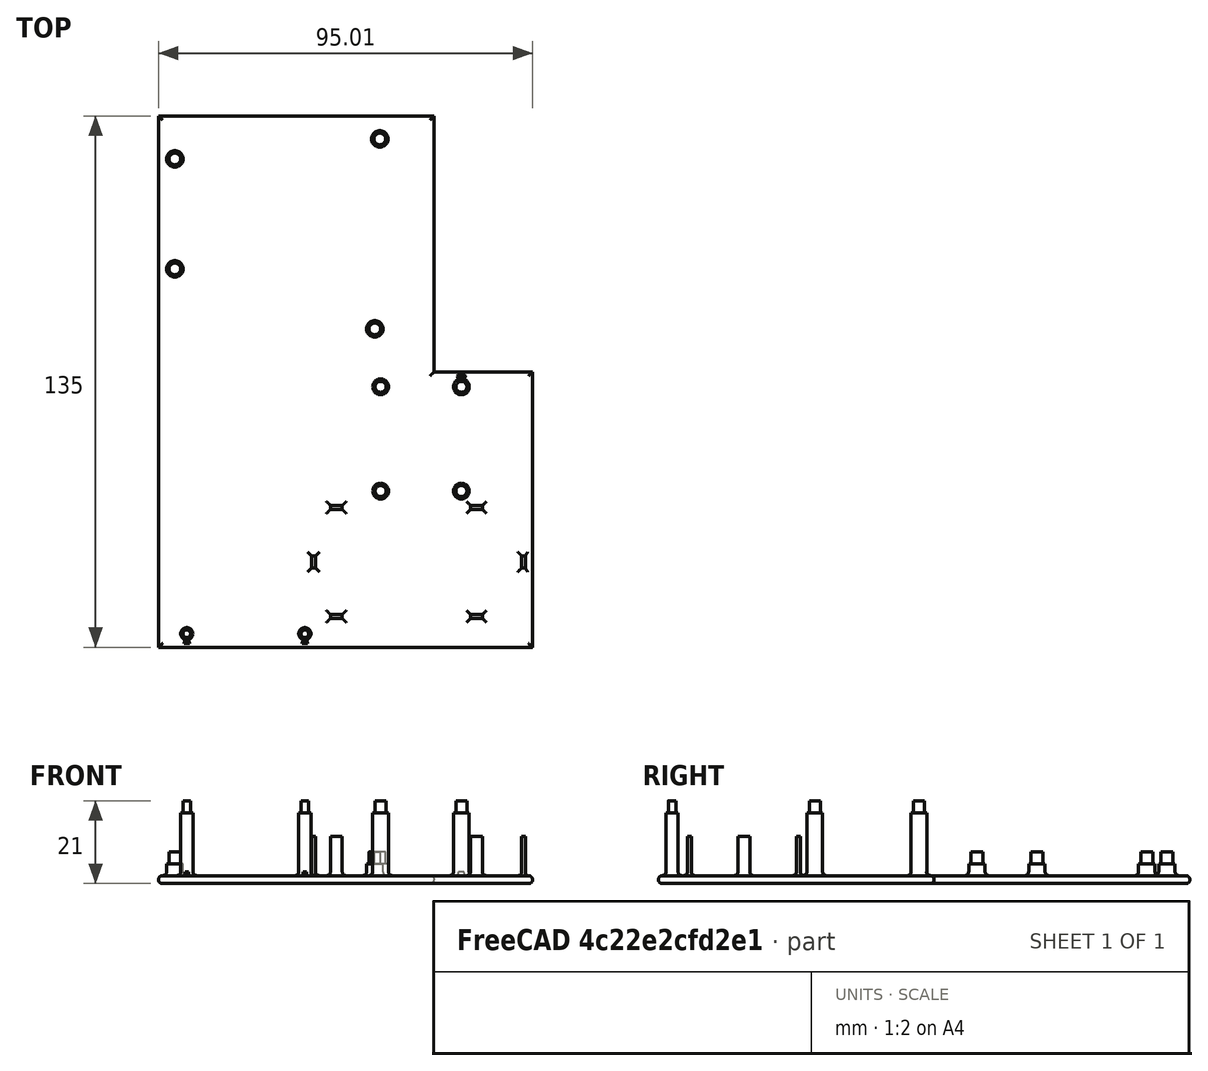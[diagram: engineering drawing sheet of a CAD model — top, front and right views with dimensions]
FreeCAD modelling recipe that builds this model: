
FCSTD DOCUMENT  (FreeCAD 2024.104R38929 (Git))
Label: arduino_tetris_platform
License: All rights reserved
objects: Part::SubShapeBinder×28, Sketcher::SketchObject×17, PartDesign::Pad×14, PartDesign::Fillet×5, PartDesign::Plane×3, PartDesign::Body×2, Mesh::Feature×2, PartDesign::Pocket×1, App::Part×1
note: 127 computed .brp shape members not serialized (recipe doc carries the construction recipe); baked Part::Feature solids carry a one-line shape summary decoded from their .brp

FEATURE [PartDesign::Plane] DatumPlane  label="PlaneBottomPlacholder"
  AttachmentOffset = pos=(0,0,4.5) rot=(0,0,1;0rad)
  InvalidShape = false
  Length = 101.325
  MapMode = 1
  MinimumLength = 10
  MinimumWidth = 10
  Placement = pos=(-3.175,-4.2,-4.295) rot=(0,0,1;0rad)
  ResizeMode = 0
  TreeRank = 432
  ValidateShape = false
  Width = 184.339
FEATURE [Sketcher::SketchObject] Sketch001
  ArcFitTolerance = 1e-06
  AttachmentSupport = -> [DatumPlane]
  ExternalBSplineMaxDegree = 5
  ExternalBSplineTolerance = 0.0001
  FullyConstrained = false
  InternalTolerance = 1e-06
  InvalidShape = false
  MakeInternals = false
  MapMode = 5
  Placement = pos=(-3.175,-4.2,-4.295) rot=(0,0,1;0rad)
  Support = -> [DatumPlane]
  TreeRank = 443
  ValidateShape = false
  sketch-geometry (4):
    g0: LineSegment StartX=-107.22 StartY=0 StartZ=0 EndX=46.1072 EndY=0 EndZ=0
    g1: LineSegment StartX=46.1072 StartY=0 StartZ=0 EndX=46.1072 EndY=144.523 EndZ=0
    g2: LineSegment StartX=46.1072 StartY=144.523 StartZ=0 EndX=-107.22 EndY=144.523 EndZ=0
    g3: LineSegment StartX=-107.22 StartY=144.523 StartZ=0 EndX=-107.22 EndY=0 EndZ=0
  constraints (9):
    c: Coincident(g0,g1)
    c: Coincident(g1,g2)
    c: Coincident(g2,g3)
    c: Coincident(g3,g0)
    c: Horizontal(g0)
    c: Horizontal(g2)
    c: Vertical(g1)
    c: Vertical(g3)
    c: PointOnObject(g0,g-1)
FEATURE [PartDesign::Plane] DatumPlane001  label="PlaneTopPlaceholder"
  AttachmentOffset = pos=(0,0,16) rot=(0,0,1;0rad)
  InvalidShape = false
  Length = 101.325
  MapMode = 5
  MinimumLength = 10
  MinimumWidth = 10
  Placement = pos=(0,0,24.75) rot=(0,0,1;0rad)
  ResizeMode = 0
  TreeRank = 444
  ValidateShape = false
  Width = 184.339
FEATURE [Sketcher::SketchObject] Sketch002
  ArcFitTolerance = 1e-06
  AttachmentSupport = -> [DatumPlane001]
  ExternalBSplineMaxDegree = 5
  ExternalBSplineTolerance = 0.0001
  FullyConstrained = false
  InternalTolerance = 1e-06
  InvalidShape = false
  MakeInternals = false
  MapMode = 5
  Placement = pos=(0,0,24.75) rot=(0,0,1;0rad)
  Support = -> [DatumPlane001]
  TreeRank = 445
  ValidateShape = false
  sketch-geometry (4):
    g0: LineSegment StartX=-110.57 StartY=-4.40204 StartZ=0 EndX=43.0268 EndY=-4.40204 EndZ=0
    g1: LineSegment StartX=43.0268 StartY=-4.40204 StartZ=0 EndX=43.0268 EndY=140.417 EndZ=0
    g2: LineSegment StartX=43.0268 StartY=140.417 StartZ=0 EndX=-110.57 EndY=140.417 EndZ=0
    g3: LineSegment StartX=-110.57 StartY=140.417 StartZ=0 EndX=-110.57 EndY=-4.40204 EndZ=0
  constraints (8):
    c: Coincident(g0,g1)
    c: Coincident(g1,g2)
    c: Coincident(g2,g3)
    c: Coincident(g3,g0)
    c: Horizontal(g0)
    c: Horizontal(g2)
    c: Vertical(g1)
    c: Vertical(g3)
FEATURE [PartDesign::Body] Body001  label="Visualisation"
  AutoGroupSolids = false
  ClaimAllChildren = false
  ExportMode = 0
  Group = -> [Sketch001,Sketch002]
  InvalidShape = false
  Origin = -> Origin010
  TreeRank = 442
  ValidateShape = false
  _ExportChildren = -> [Sketch001,Sketch002]
  _GroupVersion = 1
FEATURE [PartDesign::Plane] DatumPlane002  label="PlaneBottom"
  AttachmentOffset = pos=(0,0,-2) rot=(0,0,1;0rad)
  AttachmentSupport = -> [DatumPlane]
  InvalidShape = false
  Length = 101.325
  MapMode = 5
  MinimumLength = 10
  MinimumWidth = 10
  Placement = pos=(-3.175,-4.2,-6.295) rot=(0,0,1;0rad)
  ResizeMode = 0
  Support = -> [DatumPlane]
  TreeRank = 477
  ValidateShape = false
  Width = 184.339
FEATURE [Sketcher::SketchObject] Sketch005
  ArcFitTolerance = 1e-06
  AttachmentSupport = -> [DatumPlane002]
  ExternalBSplineMaxDegree = 5
  ExternalBSplineTolerance = 0.0001
  FullyConstrained = true
  InternalTolerance = 1e-06
  InvalidShape = false
  MakeInternals = false
  MapMode = 5
  Placement = pos=(-3.175,-4.2,-6.295) rot=(0,0,1;0rad)
  Support = -> [DatumPlane002]
  TreeRank = 491
  ValidateShape = false
  sketch-geometry (4):
    g0: LineSegment StartX=0 StartY=0 StartZ=0 EndX=95 EndY=0 EndZ=0
    g1: LineSegment StartX=95 StartY=0 StartZ=0 EndX=95 EndY=135 EndZ=0
    g2: LineSegment StartX=95 StartY=135 StartZ=0 EndX=0 EndY=135 EndZ=0
    g3: LineSegment StartX=0 StartY=135 StartZ=0 EndX=0 EndY=0 EndZ=0
  constraints (11):
    c: Coincident(g0,g1)
    c: Coincident(g1,g2)
    c: Coincident(g2,g3)
    c: Coincident(g3,g0)
    c: Horizontal(g0)
    c: Horizontal(g2)
    c: Vertical(g1)
    c: Vertical(g3)
    c: Coincident(g0,g-1)
    c: DistanceX(g2,g2) = 95
    c: DistanceY(g1,g1) = 135
FEATURE [PartDesign::Pad] Pad002
  AddSubType = 0
  AlongSketchNormal = false
  AutoTaperInnerAngle = true
  CheckUpToFaceLimits = true
  ClaimChildren = false
  Direction = (0,0,1)
  Fit = 0
  FitJoin = 0
  InnerFit = 0
  InnerFitJoin = 0
  InvalidShape = false
  Length = 2
  Length2 = 10
  Linearize = true
  NewSolid = false
  Profile = -> Sketch005
  ReferenceAxis = -> Sketch005 [N_Axis]
  Suppress = false
  TaperInnerAngle = 0
  TaperInnerAngleRev = 0
  TreeRank = 492
  Type = 0
  ValidateShape = false
  _ProfileBasedVersion = 1
FEATURE [Part::SubShapeBinder] Import  label="Import(1e77-TFT-160x128)"
  BindCopyOnChange = 0
  BindMode = 0
  ClaimChildren = false
  Context = -> Part010 [Body003.Import.]
  EdgeTolerance = 1e-06
  FillStyle = 0
  Fuse = false
  InvalidShape = false
  MakeFace = false
  MergeEdges = true
  OffsetFill = false
  OffsetIntersection = false
  OffsetJoinType = 0
  OffsetOpenResult = false
  Outline = false
  PartialLoad = false
  Relative = true
  SplitEdges = false
  TightBound = false
  TreeRank = 494
  ValidateShape = false
  _Version = 8
FEATURE [Part::SubShapeBinder] Import001  label="Import001(1e77-TFT-160x128)"
  BindCopyOnChange = 0
  BindMode = 0
  ClaimChildren = false
  Context = -> Part010 [Body003.Import001.]
  EdgeTolerance = 1e-06
  FillStyle = 0
  Fuse = false
  InvalidShape = false
  MakeFace = false
  MergeEdges = true
  OffsetFill = false
  OffsetIntersection = false
  OffsetJoinType = 0
  OffsetOpenResult = false
  Outline = false
  PartialLoad = false
  Relative = true
  SplitEdges = false
  TightBound = false
  TreeRank = 495
  ValidateShape = false
  _Version = 8
FEATURE [Part::SubShapeBinder] Import002  label="Import002(PCB)"
  BindCopyOnChange = 0
  BindMode = 0
  ClaimChildren = false
  Context = -> Part010 [Body003.Import002.]
  EdgeTolerance = 1e-06
  FillStyle = 0
  Fuse = false
  InvalidShape = false
  MakeFace = false
  MergeEdges = true
  OffsetFill = false
  OffsetIntersection = false
  OffsetJoinType = 0
  OffsetOpenResult = false
  Outline = false
  PartialLoad = false
  Relative = true
  SplitEdges = false
  TightBound = false
  TreeRank = 496
  ValidateShape = false
  _Version = 8
FEATURE [Part::SubShapeBinder] Import003  label="Import003(PCB)"
  BindCopyOnChange = 0
  BindMode = 0
  ClaimChildren = false
  Context = -> Part010 [Body003.Import003.]
  EdgeTolerance = 1e-06
  FillStyle = 0
  Fuse = false
  InvalidShape = false
  MakeFace = false
  MergeEdges = true
  OffsetFill = false
  OffsetIntersection = false
  OffsetJoinType = 0
  OffsetOpenResult = false
  Outline = false
  PartialLoad = false
  Relative = true
  SplitEdges = false
  TightBound = false
  TreeRank = 497
  ValidateShape = false
  _Version = 8
FEATURE [Part::SubShapeBinder] Import004  label="Import004(PCB)"
  BindCopyOnChange = 0
  BindMode = 0
  ClaimChildren = false
  Context = -> Part010 [Body003.Import004.]
  EdgeTolerance = 1e-06
  FillStyle = 0
  Fuse = false
  InvalidShape = false
  MakeFace = false
  MergeEdges = true
  OffsetFill = false
  OffsetIntersection = false
  OffsetJoinType = 0
  OffsetOpenResult = false
  Outline = false
  PartialLoad = false
  Relative = true
  SplitEdges = false
  TightBound = false
  TreeRank = 498
  ValidateShape = false
  _Version = 8
FEATURE [Part::SubShapeBinder] Import005  label="Import005(PCB)"
  BindCopyOnChange = 0
  BindMode = 0
  ClaimChildren = false
  Context = -> Part010 [Body003.Import005.]
  EdgeTolerance = 1e-06
  FillStyle = 0
  Fuse = false
  InvalidShape = false
  MakeFace = false
  MergeEdges = true
  OffsetFill = false
  OffsetIntersection = false
  OffsetJoinType = 0
  OffsetOpenResult = false
  Outline = false
  PartialLoad = false
  Relative = true
  SplitEdges = false
  TightBound = false
  TreeRank = 499
  ValidateShape = false
  _Version = 8
FEATURE [Sketcher::SketchObject] Sketch006
  ArcFitTolerance = 1e-06
  AttachmentSupport = -> [Pad002]
  ExternalBSplineMaxDegree = 5
  ExternalBSplineTolerance = 0.0001
  ExternalGeometry = -> [Import,Import001,Import002,Import003,Import004,Import005]
  FullyConstrained = true
  InternalTolerance = 1e-06
  InvalidShape = false
  MakeInternals = false
  MapMode = 5
  Placement = pos=(0,0,-4.295) rot=(0,0,1;0rad)
  Support = -> [Pad002]
  TreeRank = 514
  ValidateShape = false
  sketch-geometry (18):
    g0: Circle CenterX=4 CenterY=-0.75 CenterZ=0 NormalX=0 NormalY=0 NormalZ=1 AngleXU=0 Radius=1.55
    g1: Circle CenterX=34 CenterY=-0.75 CenterZ=0 NormalX=0 NormalY=0 NormalZ=1 AngleXU=0 Radius=1.55
    g2: Circle CenterX=53.25 CenterY=35.5 CenterZ=0 NormalX=0 NormalY=0 NormalZ=1 AngleXU=0 Radius=2
    g3: Circle CenterX=53.25 CenterY=62 CenterZ=0 NormalX=0 NormalY=0 NormalZ=1 AngleXU=0 Radius=2
    g4: Circle CenterX=73.75 CenterY=62 CenterZ=0 NormalX=0 NormalY=0 NormalZ=1 AngleXU=0 Radius=2
    g5: Circle CenterX=73.75 CenterY=35.5 CenterZ=0 NormalX=0 NormalY=0 NormalZ=1 AngleXU=0 Radius=2
    g6: GeomPoint [constr] X=5.55 Y=-0.75 Z=0
    g7: GeomPoint [constr] X=5.05 Y=-0.75 Z=0
    g8: GeomPoint [constr] X=35.55 Y=-0.75 Z=0
    g9: GeomPoint [constr] X=35.05 Y=-0.75 Z=0
    g10: GeomPoint [constr] X=55.25 Y=35.5 Z=0
    g11: GeomPoint [constr] X=54.75 Y=35.5 Z=0
    g12: GeomPoint [constr] X=75.75 Y=35.5 Z=0
    g13: GeomPoint [constr] X=75.25 Y=35.5 Z=0
    g14: GeomPoint [constr] X=75.75 Y=62 Z=0
    g15: GeomPoint [constr] X=75.25 Y=62 Z=0
    g16: GeomPoint [constr] X=55.25 Y=62 Z=0
    g17: GeomPoint [constr] X=54.75 Y=62 Z=0
  constraints (36):
    c: Coincident(g-3,g0)
    c: Coincident(g1,g-4)
    c: Coincident(g-5,g2)
    c: Coincident(g5,g-6)
    c: Coincident(g4,g-7)
    c: Coincident(g3,g-8)
    c: PointOnObject(g6,g0)
    c: PointOnObject(g7,g-3)
    c: Horizontal(g0,g6)
    c: Horizontal(g6,g7)
    c: PointOnObject(g8,g1)
    c: PointOnObject(g9,g-4)
    c: Horizontal(g8,g9)
    c: Horizontal(g9,g1)
    c: PointOnObject(g10,g2)
    c: PointOnObject(g11,g-5)
    c: Horizontal(g11,g10)
    c: Horizontal(g10,g2)
    c: PointOnObject(g12,g5)
    c: PointOnObject(g13,g-6)
    c: Horizontal(g13,g12)
    c: Horizontal(g12,g5)
    c: PointOnObject(g14,g4)
    c: PointOnObject(g15,g-7)
    c: Horizontal(g15,g14)
    c: Horizontal(g14,g4)
    c: PointOnObject(g16,g3)
    c: PointOnObject(g17,g-8)
    c: Horizontal(g17,g16)
    c: Horizontal(g16,g3)
    c: DistanceX(g7,g6) = 0.5
    c: DistanceX(g9,g8) = 0.5
    c: DistanceX(g11,g10) = 0.5
    c: DistanceX(g13,g12) = 0.5
    c: DistanceX(g15,g14) = 0.5
    c: DistanceX(g17,g16) = 0.5
FEATURE [Part::SubShapeBinder] Import006  label="Import006(arduino_uno)"
  BindCopyOnChange = 0
  BindMode = 0
  ClaimChildren = false
  Context = -> Part010 [Body003.Import006.]
  EdgeTolerance = 1e-06
  FillStyle = 0
  Fuse = false
  InvalidShape = false
  MakeFace = false
  MergeEdges = true
  OffsetFill = false
  OffsetIntersection = false
  OffsetJoinType = 0
  OffsetOpenResult = false
  Outline = false
  PartialLoad = false
  Relative = true
  SplitEdges = false
  TightBound = false
  TreeRank = 500
  ValidateShape = false
  _Version = 8
FEATURE [Part::SubShapeBinder] Import007  label="Import007(arduino_uno)"
  BindCopyOnChange = 0
  BindMode = 0
  ClaimChildren = false
  Context = -> Part010 [Body003.Import007.]
  EdgeTolerance = 1e-06
  FillStyle = 0
  Fuse = false
  InvalidShape = false
  MakeFace = false
  MergeEdges = true
  OffsetFill = false
  OffsetIntersection = false
  OffsetJoinType = 0
  OffsetOpenResult = false
  Outline = false
  PartialLoad = false
  Relative = true
  SplitEdges = false
  TightBound = false
  TreeRank = 501
  ValidateShape = false
  _Version = 8
FEATURE [Part::SubShapeBinder] Import008  label="Import008(arduino_uno)"
  BindCopyOnChange = 0
  BindMode = 0
  ClaimChildren = false
  Context = -> Part010 [Body003.Import008.]
  EdgeTolerance = 1e-06
  FillStyle = 0
  Fuse = false
  InvalidShape = false
  MakeFace = false
  MergeEdges = true
  OffsetFill = false
  OffsetIntersection = false
  OffsetJoinType = 0
  OffsetOpenResult = false
  Outline = false
  PartialLoad = false
  Relative = true
  SplitEdges = false
  TightBound = false
  TreeRank = 502
  ValidateShape = false
  _Version = 8
FEATURE [Part::SubShapeBinder] Import009  label="Import009(arduino_uno)"
  BindCopyOnChange = 0
  BindMode = 0
  ClaimChildren = false
  Context = -> Part010 [Body003.Import009.]
  EdgeTolerance = 1e-06
  FillStyle = 0
  Fuse = false
  InvalidShape = false
  MakeFace = false
  MergeEdges = true
  OffsetFill = false
  OffsetIntersection = false
  OffsetJoinType = 0
  OffsetOpenResult = false
  Outline = false
  PartialLoad = false
  Relative = true
  SplitEdges = false
  TightBound = false
  TreeRank = 503
  ValidateShape = false
  _Version = 8
FEATURE [Part::SubShapeBinder] Import010  label="Import010(9V_Battery)"
  BindCopyOnChange = 0
  BindMode = 0
  ClaimChildren = false
  Context = -> Part010 [Body003.Import010.]
  EdgeTolerance = 1e-06
  FillStyle = 0
  Fuse = false
  InvalidShape = false
  MakeFace = false
  MergeEdges = true
  OffsetFill = false
  OffsetIntersection = false
  OffsetJoinType = 0
  OffsetOpenResult = false
  Outline = false
  PartialLoad = false
  Relative = true
  SplitEdges = false
  TightBound = false
  TreeRank = 504
  ValidateShape = false
  _Version = 8
FEATURE [Part::SubShapeBinder] Import011  label="Import011(9V Battery Clip Connector)"
  BindCopyOnChange = 0
  BindMode = 0
  ClaimChildren = false
  Context = -> Part010 [Body003.Import011.]
  EdgeTolerance = 1e-06
  FillStyle = 0
  Fuse = false
  InvalidShape = false
  MakeFace = false
  MergeEdges = true
  OffsetFill = false
  OffsetIntersection = false
  OffsetJoinType = 0
  OffsetOpenResult = false
  Outline = false
  PartialLoad = false
  Relative = true
  SplitEdges = false
  TightBound = false
  TreeRank = 505
  ValidateShape = false
  _Version = 8
FEATURE [Part::SubShapeBinder] Import012  label="Import012(9V_Battery)"
  BindCopyOnChange = 0
  BindMode = 0
  ClaimChildren = false
  Context = -> Part010 [Body003.Import012.]
  EdgeTolerance = 1e-06
  FillStyle = 0
  Fuse = false
  InvalidShape = false
  MakeFace = false
  MergeEdges = true
  OffsetFill = false
  OffsetIntersection = false
  OffsetJoinType = 0
  OffsetOpenResult = false
  Outline = false
  PartialLoad = false
  Relative = true
  SplitEdges = false
  TightBound = false
  TreeRank = 506
  ValidateShape = false
  _Version = 8
FEATURE [Part::SubShapeBinder] Import013  label="Import013(9V_Battery)"
  BindCopyOnChange = 0
  BindMode = 0
  ClaimChildren = false
  Context = -> Part010 [Body003.Import013.]
  EdgeTolerance = 1e-06
  FillStyle = 0
  Fuse = false
  InvalidShape = false
  MakeFace = false
  MergeEdges = true
  OffsetFill = false
  OffsetIntersection = false
  OffsetJoinType = 0
  OffsetOpenResult = false
  Outline = false
  PartialLoad = false
  Relative = true
  SplitEdges = false
  TightBound = false
  TreeRank = 507
  ValidateShape = false
  _Version = 8
FEATURE [Sketcher::SketchObject] Sketch007
  ArcFitTolerance = 1e-06
  AttachmentSupport = -> [Pad002]
  ExternalBSplineMaxDegree = 5
  ExternalBSplineTolerance = 0.0001
  ExternalGeometry = -> [Import006,Import007,Import008,Import009]
  FullyConstrained = true
  InternalTolerance = 1e-06
  InvalidShape = false
  MakeInternals = false
  MapMode = 5
  Placement = pos=(0,0,-4.295) rot=(0,0,1;0rad)
  Support = -> [Pad002]
  TreeRank = 513
  ValidateShape = false
  sketch-geometry (8):
    g0: Circle CenterX=51.76 CenterY=76.7 CenterZ=0 NormalX=0 NormalY=0 NormalZ=1 AngleXU=0 Radius=2.0875
    g1: Circle CenterX=0.96 CenterY=91.94 CenterZ=0 NormalX=0 NormalY=0 NormalZ=1 AngleXU=0 Radius=2.0875
    g2: Circle CenterX=0.96 CenterY=119.88 CenterZ=0 NormalX=0 NormalY=0 NormalZ=1 AngleXU=0 Radius=2.0875
    g3: Circle CenterX=53.03 CenterY=124.96 CenterZ=0 NormalX=0 NormalY=0 NormalZ=1 AngleXU=0 Radius=2.0875
    g4: GeomPoint [constr] X=53.8475 Y=76.7 Z=0
    g5: GeomPoint [constr] X=3.0475 Y=91.94 Z=0
    g6: GeomPoint [constr] X=3.0475 Y=119.88 Z=0
    g7: GeomPoint [constr] X=55.1175 Y=124.96 Z=0
  constraints (16):
    c: Coincident(g-3,g0)
    c: Coincident(g-6,g3)
    c: Coincident(g2,g-5)
    c: Coincident(g-4,g1)
    c: PointOnObject(g4,g0)
    c: Horizontal(g4,g-3)
    c: PointOnObject(g5,g1)
    c: Horizontal(g5,g-4)
    c: PointOnObject(g6,g2)
    c: Horizontal(g6,g-5)
    c: PointOnObject(g7,g3)
    c: Horizontal(g7,g-6)
    c: DistanceX(g-3,g4) = 0.5
    c: DistanceX(g-6,g7) = 0.5
    c: DistanceX(g-4,g5) = 0.5
    c: DistanceX(g-5,g6) = 0.5
FEATURE [PartDesign::Pad] Pad003
  AddSubType = 0
  AlongSketchNormal = false
  AutoTaperInnerAngle = true
  BaseFeature = -> Pad002
  CheckUpToFaceLimits = true
  ClaimChildren = false
  Direction = (0,0,1)
  Fit = 0
  FitJoin = 0
  InnerFit = 0
  InnerFitJoin = 0
  InvalidShape = false
  Length = 16
  Length2 = 10
  Linearize = true
  NewSolid = false
  Profile = -> Sketch006
  ReferenceAxis = -> Sketch006 [N_Axis]
  Suppress = false
  TaperInnerAngle = 0
  TaperInnerAngleRev = 0
  TreeRank = 515
  Type = 0
  ValidateShape = false
  _ProfileBasedVersion = 1
FEATURE [PartDesign::Pad] Pad004
  AddSubType = 0
  AlongSketchNormal = false
  AutoTaperInnerAngle = true
  BaseFeature = -> Pad003
  CheckUpToFaceLimits = true
  ClaimChildren = false
  Direction = (0,0,1)
  Fit = 0
  FitJoin = 0
  InnerFit = 0
  InnerFitJoin = 0
  InvalidShape = false
  Length = 3
  Length2 = 10
  Linearize = true
  NewSolid = false
  Profile = -> Sketch007
  ReferenceAxis = -> Sketch007 [N_Axis]
  Suppress = false
  TaperInnerAngle = 0
  TaperInnerAngleRev = 0
  TreeRank = 516
  Type = 0
  ValidateShape = false
  _ProfileBasedVersion = 1
FEATURE [Part::SubShapeBinder] Import014  label="Import014(9V_Battery)"
  BindCopyOnChange = 0
  BindMode = 0
  ClaimChildren = false
  Context = -> Part010 [Body003.Import014.]
  EdgeTolerance = 1e-06
  FillStyle = 0
  Fuse = false
  InvalidShape = false
  MakeFace = false
  MergeEdges = true
  OffsetFill = false
  OffsetIntersection = false
  OffsetJoinType = 0
  OffsetOpenResult = false
  Outline = false
  PartialLoad = false
  Relative = true
  SplitEdges = false
  TightBound = false
  TreeRank = 518
  ValidateShape = false
  _Version = 8
FEATURE [Part::SubShapeBinder] Import015  label="Import015(9V_Battery)"
  BindCopyOnChange = 0
  BindMode = 0
  ClaimChildren = false
  Context = -> Part010 [Body003.Import015.]
  EdgeTolerance = 1e-06
  FillStyle = 0
  Fuse = false
  InvalidShape = false
  MakeFace = false
  MergeEdges = true
  OffsetFill = false
  OffsetIntersection = false
  OffsetJoinType = 0
  OffsetOpenResult = false
  Outline = false
  PartialLoad = false
  Relative = true
  SplitEdges = false
  TightBound = false
  TreeRank = 519
  ValidateShape = false
  _Version = 8
FEATURE [Part::SubShapeBinder] Import016  label="Import016(9V_Battery)"
  BindCopyOnChange = 0
  BindMode = 0
  ClaimChildren = false
  Context = -> Part010 [Body003.Import016.]
  EdgeTolerance = 1e-06
  FillStyle = 0
  Fuse = false
  InvalidShape = false
  MakeFace = false
  MergeEdges = true
  OffsetFill = false
  OffsetIntersection = false
  OffsetJoinType = 0
  OffsetOpenResult = false
  Outline = false
  PartialLoad = false
  Relative = true
  SplitEdges = false
  TightBound = false
  TreeRank = 520
  ValidateShape = false
  _Version = 8
FEATURE [Part::SubShapeBinder] Import017  label="Import017(9V Battery Clip Connector)"
  BindCopyOnChange = 0
  BindMode = 0
  ClaimChildren = false
  Context = -> Part010 [Body003.Import017.]
  EdgeTolerance = 1e-06
  FillStyle = 0
  Fuse = false
  InvalidShape = false
  MakeFace = false
  MergeEdges = true
  OffsetFill = false
  OffsetIntersection = false
  OffsetJoinType = 0
  OffsetOpenResult = false
  Outline = false
  PartialLoad = false
  Relative = true
  SplitEdges = false
  TightBound = false
  TreeRank = 521
  ValidateShape = false
  _Version = 8
FEATURE [Sketcher::SketchObject] Sketch008
  ArcFitTolerance = 1e-06
  AttachmentSupport = -> [Pad004]
  ExternalBSplineMaxDegree = 5
  ExternalBSplineTolerance = 0.0001
  ExternalGeometry = -> [Import014,Import015,Import016,Import017]
  FullyConstrained = true
  InternalTolerance = 1e-06
  InvalidShape = false
  MakeInternals = false
  MapMode = 5
  Placement = pos=(0,0,-4.295) rot=(0,0,1;0rad)
  Support = -> [Pad004]
  TreeRank = 517
  ValidateShape = false
  sketch-geometry (27):
    g0: LineSegment StartX=40.5 StartY=31.85 StartZ=0 EndX=43.5 EndY=31.85 EndZ=0
    g1: LineSegment StartX=43.5 StartY=31.85 StartZ=0 EndX=43.5 EndY=30.85 EndZ=0
    g2: LineSegment StartX=43.5 StartY=30.85 StartZ=0 EndX=40.5 EndY=30.85 EndZ=0
    g3: LineSegment StartX=40.5 StartY=30.85 StartZ=0 EndX=40.5 EndY=31.85 EndZ=0
    g4: LineSegment StartX=76.1 StartY=31.85 StartZ=0 EndX=79.1 EndY=31.85 EndZ=0
    g5: LineSegment StartX=79.1 StartY=31.85 StartZ=0 EndX=79.1 EndY=30.85 EndZ=0
    g6: LineSegment StartX=79.1 StartY=30.85 StartZ=0 EndX=76.1 EndY=30.85 EndZ=0
    g7: LineSegment StartX=76.1 StartY=30.85 StartZ=0 EndX=76.1 EndY=31.85 EndZ=0
    g8: LineSegment StartX=90.1 StartY=19 StartZ=0 EndX=89.1 EndY=19 EndZ=0
    g9: LineSegment StartX=89.1 StartY=19 StartZ=0 EndX=89.1 EndY=16 EndZ=0
    g10: LineSegment StartX=89.1 StartY=16 StartZ=0 EndX=90.1 EndY=16 EndZ=0
    g11: LineSegment StartX=90.1 StartY=16 StartZ=0 EndX=90.1 EndY=19 EndZ=0
    g12: LineSegment StartX=79.1 StartY=3.15 StartZ=0 EndX=76.1 EndY=3.15 EndZ=0
    g13: LineSegment StartX=76.1 StartY=3.15 StartZ=0 EndX=76.1 EndY=4.15 EndZ=0
    g14: LineSegment StartX=76.1 StartY=4.15 StartZ=0 EndX=79.1 EndY=4.15 EndZ=0
    g15: LineSegment StartX=79.1 StartY=4.15 StartZ=0 EndX=79.1 EndY=3.15 EndZ=0
    g16: LineSegment StartX=43.5 StartY=3.15 StartZ=0 EndX=40.5 EndY=3.15 EndZ=0
    g17: LineSegment StartX=40.5 StartY=3.15 StartZ=0 EndX=40.5 EndY=4.15 EndZ=0
    g18: LineSegment StartX=40.5 StartY=4.15 StartZ=0 EndX=43.5 EndY=4.15 EndZ=0
    g19: LineSegment StartX=43.5 StartY=4.15 StartZ=0 EndX=43.5 EndY=3.15 EndZ=0
    g20: LineSegment StartX=35.7 StartY=19 StartZ=0 EndX=36.7 EndY=19 EndZ=0
    g21: LineSegment StartX=36.7 StartY=16 StartZ=0 EndX=35.7 EndY=16 EndZ=0
    g22: LineSegment StartX=35.7 StartY=16 StartZ=0 EndX=35.7 EndY=19 EndZ=0
    g23: LineSegment [constr] StartX=37.5 StartY=28.05 StartZ=0 EndX=37.5 EndY=17.5 EndZ=0
    g24: LineSegment [constr] StartX=37.5 StartY=17.5 StartZ=0 EndX=37.5 EndY=6.95 EndZ=0
    g25: LineSegment StartX=36.7 StartY=19 StartZ=0 EndX=36.7 EndY=17.5 EndZ=0
    g26: LineSegment StartX=36.7 StartY=17.5 StartZ=0 EndX=36.7 EndY=16 EndZ=0
  constraints (80):
    c: Coincident(g0,g1)
    c: Coincident(g1,g2)
    c: Coincident(g2,g3)
    c: Coincident(g3,g0)
    c: Horizontal(g0)
    c: Horizontal(g2)
    c: Vertical(g1)
    c: Vertical(g3)
    c: Coincident(g4,g5)
    c: Coincident(g5,g6)
    c: Coincident(g6,g7)
    c: Coincident(g7,g4)
    c: Horizontal(g4)
    c: Horizontal(g6)
    c: Vertical(g5)
    c: Vertical(g7)
    c: Coincident(g8,g9)
    c: Coincident(g9,g10)
    c: Coincident(g10,g11)
    c: Coincident(g11,g8)
    c: Horizontal(g8)
    c: Horizontal(g10)
    c: Vertical(g9)
    c: Vertical(g11)
    c: Coincident(g12,g13)
    c: Coincident(g13,g14)
    c: Coincident(g14,g15)
    c: Coincident(g15,g12)
    c: Horizontal(g12)
    c: Horizontal(g14)
    c: Vertical(g13)
    c: Vertical(g15)
    c: Coincident(g16,g17)
    c: Coincident(g17,g18)
    c: Coincident(g18,g19)
    c: Coincident(g19,g16)
    c: Horizontal(g16)
    c: Horizontal(g18)
    c: Vertical(g17)
    c: Vertical(g19)
    c: Coincident(g20,g25)
    c: Coincident(g26,g21)
    c: Coincident(g21,g22)
    c: Coincident(g22,g20)
    c: Horizontal(g20)
    c: Horizontal(g21)
    c: Vertical(g22)
    c: Equal(g3,g7)
    c: Equal(g7,g8)
    c: Equal(g8,g13)
    c: Equal(g13,g17)
    c: Equal(g17,g20)
    c: Equal(g18,g14)
    c: Equal(g14,g6)
    c: Equal(g6,g9)
    c: Vertical(g5,g14)
    c: Vertical(g18,g1)
    c: Horizontal(g20,g8)
    c: Coincident(g23,g-3)
    c: Coincident(g24,g-3)
    c: Coincident(g23,g24)
    c: PointOnObject(g23,g-3)
    c: Equal(g23,g24)
    c: DistanceX(g16,g16) = 3
    c: DistanceY(g19,g19) = 1
    c: DistanceX(g-3,g17) = 3
    c: DistanceX(g14,g-5) = 3
    c: Horizontal(g18,g13)
    c: Horizontal(g1,g6)
    c: DistanceY(g14,g-5) = 0.1
    c: DistanceY(g-4,g5) = 0.1
    c: Coincident(g25,g26)
    c: Vertical(g25)
    c: Vertical(g26)
    c: Equal(g25,g26)
    c: Horizontal(g25,g23)
    c: Equal(g0,g22)
    c: Equal(g22,g18)
    c: DistanceX(g25,g23) = 0.8
    c: DistanceX(g-6,g8) = 0.1
FEATURE [PartDesign::Pad] Pad005
  AddSubType = 0
  AlongSketchNormal = false
  AutoTaperInnerAngle = true
  BaseFeature = -> Pad004
  CheckUpToFaceLimits = true
  ClaimChildren = false
  Direction = (0,0,1)
  Fit = 0
  FitJoin = 0
  InnerFit = 0
  InnerFitJoin = 0
  InvalidShape = false
  Length = 10
  Length2 = 10
  Linearize = true
  NewSolid = false
  Profile = -> Sketch008
  ReferenceAxis = -> Sketch008 [N_Axis]
  Suppress = false
  TaperInnerAngle = 0
  TaperInnerAngleRev = 0
  TreeRank = 522
  Type = 0
  ValidateShape = false
  _ProfileBasedVersion = 1
FEATURE [Part::SubShapeBinder] Import018  label="Import018(1e77-TFT-160x128)"
  BindCopyOnChange = 0
  BindMode = 0
  ClaimChildren = false
  Context = -> Part010 [Body003.Import018.]
  EdgeTolerance = 1e-06
  FillStyle = 0
  Fuse = false
  InvalidShape = false
  MakeFace = false
  MergeEdges = true
  OffsetFill = false
  OffsetIntersection = false
  OffsetJoinType = 0
  OffsetOpenResult = false
  Outline = false
  PartialLoad = false
  Relative = true
  SplitEdges = false
  TightBound = false
  TreeRank = 524
  ValidateShape = false
  _Version = 8
FEATURE [Sketcher::SketchObject] Sketch009
  ArcFitTolerance = 1e-06
  AttachmentSupport = -> [Pad005]
  ExternalBSplineMaxDegree = 5
  ExternalBSplineTolerance = 0.0001
  ExternalGeometry = -> [Import018]
  FullyConstrained = true
  InternalTolerance = 1e-06
  InvalidShape = false
  MakeInternals = false
  MapMode = 5
  Placement = pos=(0,0,11.705) rot=(0,0,1;0rad)
  Support = -> [Pad005]
  TreeRank = 523
  ValidateShape = false
  sketch-geometry (3):
    g0: Circle CenterX=4 CenterY=-0.75 CenterZ=0 NormalX=0 NormalY=0 NormalZ=1 AngleXU=0 Radius=0.95
    g1: GeomPoint [constr] X=4.95 Y=-0.75 Z=0
    g2: GeomPoint [constr] X=5.05 Y=-0.75 Z=0
  constraints (6):
    c: Coincident(g0,g-3)
    c: PointOnObject(g1,g0)
    c: PointOnObject(g2,g-3)
    c: Horizontal(g2,g1)
    c: Horizontal(g1,g0)
    c: DistanceX(g1,g2) = 0.1
FEATURE [Part::SubShapeBinder] Import019  label="Import019(1e77-TFT-160x128)"
  BindCopyOnChange = 0
  BindMode = 0
  ClaimChildren = false
  Context = -> Part010 [Body003.Import019.]
  EdgeTolerance = 1e-06
  FillStyle = 0
  Fuse = false
  InvalidShape = false
  MakeFace = false
  MergeEdges = true
  OffsetFill = false
  OffsetIntersection = false
  OffsetJoinType = 0
  OffsetOpenResult = false
  Outline = false
  PartialLoad = false
  Relative = true
  SplitEdges = false
  TightBound = false
  TreeRank = 526
  ValidateShape = false
  _Version = 8
FEATURE [Sketcher::SketchObject] Sketch010
  ArcFitTolerance = 1e-06
  AttachmentSupport = -> [Pad005]
  ExternalBSplineMaxDegree = 5
  ExternalBSplineTolerance = 0.0001
  ExternalGeometry = -> [Import019]
  FullyConstrained = true
  InternalTolerance = 1e-06
  InvalidShape = false
  MakeInternals = false
  MapMode = 5
  Placement = pos=(0,0,11.705) rot=(0,0,1;0rad)
  Support = -> [Pad005]
  TreeRank = 527
  ValidateShape = false
  sketch-geometry (3):
    g0: Circle CenterX=34 CenterY=-0.75 CenterZ=0 NormalX=0 NormalY=0 NormalZ=1 AngleXU=0 Radius=0.95
    g1: GeomPoint [constr] X=34.95 Y=-0.75 Z=0
    g2: GeomPoint [constr] X=35.05 Y=-0.75 Z=0
  constraints (6):
    c: Coincident(g0,g-3)
    c: PointOnObject(g1,g0)
    c: PointOnObject(g2,g-3)
    c: Horizontal(g2,g1)
    c: Horizontal(g1,g0)
    c: DistanceX(g1,g2) = 0.1
FEATURE [PartDesign::Pad] Pad006
  AddSubType = 0
  AlongSketchNormal = false
  AutoTaperInnerAngle = true
  BaseFeature = -> Pad005
  CheckUpToFaceLimits = true
  ClaimChildren = false
  Direction = (0,0,1)
  Fit = 0
  FitJoin = 0
  InnerFit = 0
  InnerFitJoin = 0
  InvalidShape = false
  Length = 3
  Length2 = 10
  Linearize = true
  NewSolid = false
  Profile = -> Sketch009
  ReferenceAxis = -> Sketch009 [N_Axis]
  Suppress = false
  TaperInnerAngle = 0
  TaperInnerAngleRev = 0
  TreeRank = 528
  Type = 0
  ValidateShape = false
  _ProfileBasedVersion = 1
FEATURE [PartDesign::Pad] Pad007
  AddSubType = 0
  AlongSketchNormal = false
  AutoTaperInnerAngle = true
  BaseFeature = -> Pad006
  CheckUpToFaceLimits = true
  ClaimChildren = false
  Direction = (0,0,1)
  Fit = 0
  FitJoin = 0
  InnerFit = 0
  InnerFitJoin = 0
  InvalidShape = false
  Length = 3
  Length2 = 10
  Linearize = true
  NewSolid = false
  Profile = -> Sketch010
  ReferenceAxis = -> Sketch010 [N_Axis]
  Suppress = false
  TaperInnerAngle = 0
  TaperInnerAngleRev = 0
  TreeRank = 529
  Type = 0
  ValidateShape = false
  _ProfileBasedVersion = 1
FEATURE [Part::SubShapeBinder] Import020  label="Import020(PCB)"
  BindCopyOnChange = 0
  BindMode = 0
  ClaimChildren = false
  Context = -> Part010 [Body003.Import020.]
  EdgeTolerance = 1e-06
  FillStyle = 0
  Fuse = false
  InvalidShape = false
  MakeFace = false
  MergeEdges = true
  OffsetFill = false
  OffsetIntersection = false
  OffsetJoinType = 0
  OffsetOpenResult = false
  Outline = false
  PartialLoad = false
  Relative = true
  SplitEdges = false
  TightBound = false
  TreeRank = 531
  ValidateShape = false
  _Version = 8
FEATURE [Sketcher::SketchObject] Sketch011
  ArcFitTolerance = 1e-06
  AttachmentSupport = -> [Pad007]
  ExternalBSplineMaxDegree = 5
  ExternalBSplineTolerance = 0.0001
  ExternalGeometry = -> [Import020]
  FullyConstrained = true
  InternalTolerance = 1e-06
  InvalidShape = false
  MakeInternals = false
  MapMode = 5
  Placement = pos=(0,0,11.705) rot=(0,0,1;0rad)
  Support = -> [Pad007]
  TreeRank = 530
  ValidateShape = false
  sketch-geometry (3):
    g0: Circle CenterX=53.25 CenterY=35.5 CenterZ=0 NormalX=0 NormalY=0 NormalZ=1 AngleXU=0 Radius=1.4
    g1: GeomPoint [constr] X=54.75 Y=35.5 Z=0
    g2: GeomPoint [constr] X=54.65 Y=35.5 Z=0
  constraints (6):
    c: Coincident(g0,g-3)
    c: PointOnObject(g1,g-3)
    c: PointOnObject(g2,g0)
    c: Horizontal(g0,g2)
    c: Horizontal(g2,g1)
    c: DistanceX(g2,g1) = 0.1
FEATURE [PartDesign::Pad] Pad008
  AddSubType = 0
  AlongSketchNormal = false
  AutoTaperInnerAngle = true
  BaseFeature = -> Pad007
  CheckUpToFaceLimits = true
  ClaimChildren = false
  Direction = (0,0,1)
  Fit = 0
  FitJoin = 0
  InnerFit = 0
  InnerFitJoin = 0
  InvalidShape = false
  Length = 3
  Length2 = 10
  Linearize = true
  NewSolid = false
  Profile = -> Sketch011
  ReferenceAxis = -> Sketch011 [N_Axis]
  Suppress = false
  TaperInnerAngle = 0
  TaperInnerAngleRev = 0
  TreeRank = 532
  Type = 0
  ValidateShape = false
  _ProfileBasedVersion = 1
FEATURE [Part::SubShapeBinder] Import021  label="Import021(PCB)"
  BindCopyOnChange = 0
  BindMode = 0
  ClaimChildren = false
  Context = -> Part010 [Body003.Import021.]
  EdgeTolerance = 1e-06
  FillStyle = 0
  Fuse = false
  InvalidShape = false
  MakeFace = false
  MergeEdges = true
  OffsetFill = false
  OffsetIntersection = false
  OffsetJoinType = 0
  OffsetOpenResult = false
  Outline = false
  PartialLoad = false
  Relative = true
  SplitEdges = false
  TightBound = false
  TreeRank = 534
  ValidateShape = false
  _Version = 8
FEATURE [Sketcher::SketchObject] Sketch012
  ArcFitTolerance = 1e-06
  AttachmentSupport = -> [Pad008]
  ExternalBSplineMaxDegree = 5
  ExternalBSplineTolerance = 0.0001
  ExternalGeometry = -> [Import021]
  FullyConstrained = true
  InternalTolerance = 1e-06
  InvalidShape = false
  MakeInternals = false
  MapMode = 5
  Placement = pos=(0,0,11.705) rot=(0,0,1;0rad)
  Support = -> [Pad008]
  TreeRank = 533
  ValidateShape = false
  sketch-geometry (3):
    g0: Circle CenterX=73.75 CenterY=35.5 CenterZ=0 NormalX=0 NormalY=0 NormalZ=1 AngleXU=0 Radius=1.4
    g1: GeomPoint [constr] X=75.15 Y=35.5 Z=0
    g2: GeomPoint [constr] X=75.25 Y=35.5 Z=0
  constraints (6):
    c: Coincident(g0,g-3)
    c: PointOnObject(g1,g0)
    c: PointOnObject(g2,g-3)
    c: Horizontal(g2,g1)
    c: Horizontal(g1,g0)
    c: DistanceX(g1,g2) = 0.1
FEATURE [PartDesign::Pad] Pad009
  AddSubType = 0
  AlongSketchNormal = false
  AutoTaperInnerAngle = true
  BaseFeature = -> Pad008
  CheckUpToFaceLimits = true
  ClaimChildren = false
  Direction = (0,0,1)
  Fit = 0
  FitJoin = 0
  InnerFit = 0
  InnerFitJoin = 0
  InvalidShape = false
  Length = 3
  Length2 = 10
  Linearize = true
  NewSolid = false
  Profile = -> Sketch012
  ReferenceAxis = -> Sketch012 [N_Axis]
  Suppress = false
  TaperInnerAngle = 0
  TaperInnerAngleRev = 0
  TreeRank = 535
  Type = 0
  ValidateShape = false
  _ProfileBasedVersion = 1
FEATURE [Part::SubShapeBinder] Import022  label="Import022(PCB)"
  BindCopyOnChange = 0
  BindMode = 0
  ClaimChildren = false
  Context = -> Part010 [Body003.Import022.]
  EdgeTolerance = 1e-06
  FillStyle = 0
  Fuse = false
  InvalidShape = false
  MakeFace = false
  MergeEdges = true
  OffsetFill = false
  OffsetIntersection = false
  OffsetJoinType = 0
  OffsetOpenResult = false
  Outline = false
  PartialLoad = false
  Relative = true
  SplitEdges = false
  TightBound = false
  TreeRank = 537
  ValidateShape = false
  _Version = 8
FEATURE [Sketcher::SketchObject] Sketch013
  ArcFitTolerance = 1e-06
  AttachmentSupport = -> [Pad009]
  ExternalBSplineMaxDegree = 5
  ExternalBSplineTolerance = 0.0001
  ExternalGeometry = -> [Import022]
  FullyConstrained = true
  InternalTolerance = 1e-06
  InvalidShape = false
  MakeInternals = false
  MapMode = 5
  Placement = pos=(0,0,11.705) rot=(0,0,1;0rad)
  Support = -> [Pad009]
  TreeRank = 536
  ValidateShape = false
  sketch-geometry (3):
    g0: Circle CenterX=73.75 CenterY=62 CenterZ=0 NormalX=0 NormalY=0 NormalZ=1 AngleXU=0 Radius=1.4
    g1: GeomPoint [constr] X=75.15 Y=62 Z=0
    g2: GeomPoint [constr] X=75.25 Y=62 Z=0
  constraints (6):
    c: Coincident(g0,g-3)
    c: PointOnObject(g1,g0)
    c: PointOnObject(g2,g-3)
    c: Horizontal(g2,g1)
    c: Horizontal(g1,g0)
    c: DistanceX(g1,g2) = 0.1
FEATURE [PartDesign::Pad] Pad010
  AddSubType = 0
  AlongSketchNormal = false
  AutoTaperInnerAngle = true
  BaseFeature = -> Pad009
  CheckUpToFaceLimits = true
  ClaimChildren = false
  Direction = (0,0,1)
  Fit = 0
  FitJoin = 0
  InnerFit = 0
  InnerFitJoin = 0
  InvalidShape = false
  Length = 3
  Length2 = 10
  Linearize = true
  NewSolid = false
  Profile = -> Sketch013
  ReferenceAxis = -> Sketch013 [N_Axis]
  Suppress = false
  TaperInnerAngle = 0
  TaperInnerAngleRev = 0
  TreeRank = 538
  Type = 0
  ValidateShape = false
  _ProfileBasedVersion = 1
FEATURE [Part::SubShapeBinder] Import023  label="Import023(PCB)"
  BindCopyOnChange = 0
  BindMode = 0
  ClaimChildren = false
  Context = -> Part010 [Body003.Import023.]
  EdgeTolerance = 1e-06
  FillStyle = 0
  Fuse = false
  InvalidShape = false
  MakeFace = false
  MergeEdges = true
  OffsetFill = false
  OffsetIntersection = false
  OffsetJoinType = 0
  OffsetOpenResult = false
  Outline = false
  PartialLoad = false
  Relative = true
  SplitEdges = false
  TightBound = false
  TreeRank = 540
  ValidateShape = false
  _Version = 8
FEATURE [Sketcher::SketchObject] Sketch014
  ArcFitTolerance = 1e-06
  AttachmentSupport = -> [Pad010]
  ExternalBSplineMaxDegree = 5
  ExternalBSplineTolerance = 0.0001
  ExternalGeometry = -> [Import023]
  FullyConstrained = true
  InternalTolerance = 1e-06
  InvalidShape = false
  MakeInternals = false
  MapMode = 5
  Placement = pos=(0,0,11.705) rot=(0,0,1;0rad)
  Support = -> [Pad010]
  TreeRank = 539
  ValidateShape = false
  sketch-geometry (3):
    g0: Circle CenterX=53.25 CenterY=62 CenterZ=0 NormalX=0 NormalY=0 NormalZ=1 AngleXU=0 Radius=1.4
    g1: GeomPoint [constr] X=54.65 Y=62 Z=0
    g2: GeomPoint [constr] X=54.75 Y=62 Z=0
  constraints (6):
    c: Coincident(g0,g-3)
    c: PointOnObject(g1,g0)
    c: PointOnObject(g2,g-3)
    c: Horizontal(g2,g1)
    c: Horizontal(g1,g0)
    c: DistanceX(g1,g2) = 0.1
FEATURE [PartDesign::Pad] Pad011
  AddSubType = 0
  AlongSketchNormal = false
  AutoTaperInnerAngle = true
  BaseFeature = -> Pad010
  CheckUpToFaceLimits = true
  ClaimChildren = false
  Direction = (0,0,1)
  Fit = 0
  FitJoin = 0
  InnerFit = 0
  InnerFitJoin = 0
  InvalidShape = false
  Length = 3
  Length2 = 10
  Linearize = true
  NewSolid = false
  Profile = -> Sketch014
  ReferenceAxis = -> Sketch014 [N_Axis]
  Suppress = false
  TaperInnerAngle = 0
  TaperInnerAngleRev = 0
  TreeRank = 541
  Type = 0
  ValidateShape = false
  _ProfileBasedVersion = 1
FEATURE [Part::SubShapeBinder] Import024  label="Import024(arduino_uno)"
  BindCopyOnChange = 0
  BindMode = 0
  ClaimChildren = false
  Context = -> Part010 [Body003.Import024.]
  EdgeTolerance = 1e-06
  FillStyle = 0
  Fuse = false
  InvalidShape = false
  MakeFace = false
  MergeEdges = true
  OffsetFill = false
  OffsetIntersection = false
  OffsetJoinType = 0
  OffsetOpenResult = false
  Outline = false
  PartialLoad = false
  Relative = true
  SplitEdges = false
  TightBound = false
  TreeRank = 543
  ValidateShape = false
  _Version = 8
FEATURE [Sketcher::SketchObject] Sketch015
  ArcFitTolerance = 1e-06
  AttachmentSupport = -> [Pad011]
  ExternalBSplineMaxDegree = 5
  ExternalBSplineTolerance = 0.0001
  ExternalGeometry = -> [Import024]
  FullyConstrained = true
  InternalTolerance = 1e-06
  InvalidShape = false
  MakeInternals = false
  MapMode = 5
  Placement = pos=(0,0,-1.295) rot=(0,0,1;0rad)
  Support = -> [Pad011]
  TreeRank = 542
  ValidateShape = false
  sketch-geometry (2):
    g0: Circle CenterX=51.76 CenterY=76.7 CenterZ=0 NormalX=0 NormalY=0 NormalZ=1 AngleXU=0 Radius=1.4875
    g1: GeomPoint [constr] X=53.2475 Y=76.7 Z=0
  constraints (4):
    c: Coincident(g0,g-3)
    c: PointOnObject(g1,g0)
    c: Horizontal(g-3,g1)
    c: DistanceX(g1,g-3) = 0.1
FEATURE [PartDesign::Pad] Pad012
  AddSubType = 0
  AlongSketchNormal = false
  AutoTaperInnerAngle = true
  BaseFeature = -> Pad011
  CheckUpToFaceLimits = true
  ClaimChildren = false
  Direction = (0,0,1)
  Fit = 0
  FitJoin = 0
  InnerFit = 0
  InnerFitJoin = 0
  InvalidShape = false
  Length = 3
  Length2 = 10
  Linearize = true
  NewSolid = false
  Profile = -> Sketch015
  ReferenceAxis = -> Sketch015 [N_Axis]
  Suppress = false
  TaperInnerAngle = 0
  TaperInnerAngleRev = 0
  TreeRank = 544
  Type = 0
  ValidateShape = false
  _ProfileBasedVersion = 1
FEATURE [Part::SubShapeBinder] Import025  label="Import025(arduino_uno)"
  BindCopyOnChange = 0
  BindMode = 0
  ClaimChildren = false
  Context = -> Part010 [Body003.Import025.]
  EdgeTolerance = 1e-06
  FillStyle = 0
  Fuse = false
  InvalidShape = false
  MakeFace = false
  MergeEdges = true
  OffsetFill = false
  OffsetIntersection = false
  OffsetJoinType = 0
  OffsetOpenResult = false
  Outline = false
  PartialLoad = false
  Relative = true
  SplitEdges = false
  TightBound = false
  TreeRank = 546
  ValidateShape = false
  _Version = 8
FEATURE [Sketcher::SketchObject] Sketch016
  ArcFitTolerance = 1e-06
  AttachmentSupport = -> [Pad012]
  ExternalBSplineMaxDegree = 5
  ExternalBSplineTolerance = 0.0001
  ExternalGeometry = -> [Import025]
  FullyConstrained = true
  InternalTolerance = 1e-06
  InvalidShape = false
  MakeInternals = false
  MapMode = 5
  Placement = pos=(0,0,-1.295) rot=(0,0,1;0rad)
  Support = -> [Pad012]
  TreeRank = 545
  ValidateShape = false
  sketch-geometry (2):
    g0: Circle CenterX=0.96 CenterY=91.94 CenterZ=0 NormalX=0 NormalY=0 NormalZ=1 AngleXU=0 Radius=1.4875
    g1: GeomPoint [constr] X=2.4475 Y=91.94 Z=0
  constraints (4):
    c: Coincident(g0,g-3)
    c: PointOnObject(g1,g0)
    c: Horizontal(g-3,g1)
    c: DistanceX(g1,g-3) = 0.1
FEATURE [PartDesign::Pad] Pad013
  AddSubType = 0
  AlongSketchNormal = false
  AutoTaperInnerAngle = true
  BaseFeature = -> Pad012
  CheckUpToFaceLimits = true
  ClaimChildren = false
  Direction = (0,0,1)
  Fit = 0
  FitJoin = 0
  InnerFit = 0
  InnerFitJoin = 0
  InvalidShape = false
  Length = 3
  Length2 = 10
  Linearize = true
  NewSolid = false
  Profile = -> Sketch016
  ReferenceAxis = -> Sketch016 [N_Axis]
  Suppress = false
  TaperInnerAngle = 0
  TaperInnerAngleRev = 0
  TreeRank = 547
  Type = 0
  ValidateShape = false
  _ProfileBasedVersion = 1
FEATURE [Part::SubShapeBinder] Import026  label="Import026(arduino_uno)"
  BindCopyOnChange = 0
  BindMode = 0
  ClaimChildren = false
  Context = -> Part010 [Body003.Import026.]
  EdgeTolerance = 1e-06
  FillStyle = 0
  Fuse = false
  InvalidShape = false
  MakeFace = false
  MergeEdges = true
  OffsetFill = false
  OffsetIntersection = false
  OffsetJoinType = 0
  OffsetOpenResult = false
  Outline = false
  PartialLoad = false
  Relative = true
  SplitEdges = false
  TightBound = false
  TreeRank = 549
  ValidateShape = false
  _Version = 8
FEATURE [Sketcher::SketchObject] Sketch017
  ArcFitTolerance = 1e-06
  AttachmentSupport = -> [Pad013]
  ExternalBSplineMaxDegree = 5
  ExternalBSplineTolerance = 0.0001
  ExternalGeometry = -> [Import026]
  FullyConstrained = true
  InternalTolerance = 1e-06
  InvalidShape = false
  MakeInternals = false
  MapMode = 5
  Placement = pos=(0,0,-1.295) rot=(0,0,1;0rad)
  Support = -> [Pad013]
  TreeRank = 548
  ValidateShape = false
  sketch-geometry (2):
    g0: Circle CenterX=0.96 CenterY=119.88 CenterZ=0 NormalX=0 NormalY=0 NormalZ=1 AngleXU=0 Radius=1.4875
    g1: GeomPoint [constr] X=2.4475 Y=119.88 Z=0
  constraints (4):
    c: Coincident(g0,g-3)
    c: PointOnObject(g1,g0)
    c: Horizontal(g-3,g1)
    c: DistanceX(g1,g-3) = 0.1
FEATURE [Part::SubShapeBinder] Import027  label="Import027(arduino_uno)"
  BindCopyOnChange = 0
  BindMode = 0
  ClaimChildren = false
  Context = -> Part010 [Body003.Import027.]
  EdgeTolerance = 1e-06
  FillStyle = 0
  Fuse = false
  InvalidShape = false
  MakeFace = false
  MergeEdges = true
  OffsetFill = false
  OffsetIntersection = false
  OffsetJoinType = 0
  OffsetOpenResult = false
  Outline = false
  PartialLoad = false
  Relative = true
  SplitEdges = false
  TightBound = false
  TreeRank = 551
  ValidateShape = false
  _Version = 8
FEATURE [Sketcher::SketchObject] Sketch018
  ArcFitTolerance = 1e-06
  AttachmentSupport = -> [Pad013]
  ExternalBSplineMaxDegree = 5
  ExternalBSplineTolerance = 0.0001
  ExternalGeometry = -> [Import027]
  FullyConstrained = true
  InternalTolerance = 1e-06
  InvalidShape = false
  MakeInternals = false
  MapMode = 5
  Placement = pos=(0,0,-1.295) rot=(0,0,1;0rad)
  Support = -> [Pad013]
  TreeRank = 550
  ValidateShape = false
  sketch-geometry (2):
    g0: Circle CenterX=53.03 CenterY=124.96 CenterZ=0 NormalX=0 NormalY=0 NormalZ=1 AngleXU=0 Radius=1.4875
    g1: GeomPoint [constr] X=54.5175 Y=124.96 Z=0
  constraints (4):
    c: Coincident(g0,g-3)
    c: PointOnObject(g1,g0)
    c: Horizontal(g1,g-3)
    c: DistanceX(g1,g-3) = 0.1
FEATURE [PartDesign::Pad] Pad014
  AddSubType = 0
  AlongSketchNormal = false
  AutoTaperInnerAngle = true
  BaseFeature = -> Pad013
  CheckUpToFaceLimits = true
  ClaimChildren = false
  Direction = (0,0,1)
  Fit = 0
  FitJoin = 0
  InnerFit = 0
  InnerFitJoin = 0
  InvalidShape = false
  Length = 3
  Length2 = 10
  Linearize = true
  NewSolid = false
  Profile = -> Sketch018
  ReferenceAxis = -> Sketch018 [N_Axis]
  Suppress = false
  TaperInnerAngle = 0
  TaperInnerAngleRev = 0
  TreeRank = 552
  Type = 0
  ValidateShape = false
  _ProfileBasedVersion = 1
FEATURE [PartDesign::Pad] Pad015
  AddSubType = 0
  AlongSketchNormal = false
  AutoTaperInnerAngle = true
  BaseFeature = -> Pad014
  CheckUpToFaceLimits = true
  ClaimChildren = false
  Direction = (0,0,1)
  Fit = 0
  FitJoin = 0
  InnerFit = 0
  InnerFitJoin = 0
  InvalidShape = false
  Length = 3
  Length2 = 10
  Linearize = true
  NewSolid = false
  Profile = -> Sketch017
  ReferenceAxis = -> Sketch017 [N_Axis]
  Suppress = false
  TaperInnerAngle = 0
  TaperInnerAngleRev = 0
  TreeRank = 553
  Type = 0
  ValidateShape = false
  _ProfileBasedVersion = 1
FEATURE [Sketcher::SketchObject] Sketch019
  ArcFitTolerance = 1e-06
  AttachmentSupport = -> [Pad015]
  ExternalBSplineMaxDegree = 5
  ExternalBSplineTolerance = 0.0001
  ExternalGeometry = -> [Pad015]
  FullyConstrained = true
  InternalTolerance = 1e-06
  InvalidShape = false
  MakeInternals = false
  MapMode = 5
  Placement = pos=(0,0,-4.295) rot=(0,0,1;0rad)
  Support = -> [Pad015]
  TreeRank = 554
  ValidateShape = false
  sketch-geometry (4):
    g0: LineSegment StartX=66.825 StartY=130.8 StartZ=0 EndX=91.825 EndY=130.8 EndZ=0
    g1: LineSegment StartX=91.825 StartY=130.8 StartZ=0 EndX=91.825 EndY=65.8 EndZ=0
    g2: LineSegment StartX=91.825 StartY=65.8 StartZ=0 EndX=66.825 EndY=65.8 EndZ=0
    g3: LineSegment StartX=66.825 StartY=65.8 StartZ=0 EndX=66.825 EndY=130.8 EndZ=0
  constraints (11):
    c: Coincident(g0,g1)
    c: Coincident(g1,g2)
    c: Coincident(g2,g3)
    c: Coincident(g3,g0)
    c: Horizontal(g0)
    c: Horizontal(g2)
    c: Vertical(g1)
    c: Vertical(g3)
    c: Coincident(g0,g-3)
    c: DistanceY(g1,g1) = 65
    c: DistanceX(g0,g0) = 25
FEATURE [PartDesign::Pocket] Pocket
  AddSubType = 1
  AlongSketchNormal = false
  AutoTaperInnerAngle = true
  BaseFeature = -> Pad015
  CheckUpToFaceLimits = true
  ClaimChildren = false
  Direction = (0,0,-1)
  Fit = 0
  FitJoin = 0
  InnerFit = 0
  InnerFitJoin = 0
  InvalidShape = false
  Length = 5
  Length2 = 10
  Linearize = true
  NewSolid = false
  Profile = -> Sketch019
  ReferenceAxis = -> Sketch019 [N_Axis]
  Suppress = false
  TaperInnerAngle = 0
  TaperInnerAngleRev = 0
  TreeRank = 555
  Type = 1
  ValidateShape = false
  _ProfileBasedVersion = 1
  _Version = 1
FEATURE [Mesh::Feature] Mesh  label="Mesh_NoFillets"
  TreeRank = 556
FEATURE [PartDesign::Fillet] Fillet
  AddSubType = 0
  Base = -> Pocket [Edge4,Edge7,Edge14,Edge15,Edge16,Edge10]
  BaseFeature = -> Pocket
  InvalidShape = false
  NewSolid = false
  Radius = 1
  SupportTransform = false
  Suppress = false
  TreeRank = 557
  UseAllEdges = false
  ValidateShape = false
FEATURE [PartDesign::Fillet] Fillet001
  AddSubType = 0
  Base = -> Fillet [Edge14,Edge3,Edge7,Edge11,Edge12,Edge13]
  BaseFeature = -> Fillet
  InvalidShape = false
  NewSolid = false
  Radius = 0.9
  SupportTransform = false
  Suppress = false
  TreeRank = 558
  UseAllEdges = false
  ValidateShape = false
FEATURE [PartDesign::Fillet] Fillet002
  AddSubType = 0
  Base = -> Fillet001 [Edge46,Edge45,Edge47,Edge48,Edge49,Edge50,Edge66,Edge67,Edge55,Edge65]
  BaseFeature = -> Fillet001
  InvalidShape = false
  NewSolid = false
  Radius = 1
  SupportTransform = false
  Suppress = false
  TreeRank = 559
  UseAllEdges = false
  ValidateShape = false
FEATURE [PartDesign::Fillet] Fillet003
  AddSubType = 0
  Base = -> Fillet002 [Edge35,Edge33,Edge34,Edge36,Edge28,Edge27,Edge26,Edge25,Edge24,Edge23,Edge21,Edge30,Edge29,Edge31,Edge32,Edge43,Edge42,Edge44,Edge45,Edge37,Edge41,Edge38,Edge39]
  BaseFeature = -> Fillet002
  InvalidShape = false
  NewSolid = false
  Radius = 1
  SupportTransform = false
  Suppress = false
  TreeRank = 560
  UseAllEdges = false
  ValidateShape = false
FEATURE [PartDesign::Fillet] Fillet004
  AddSubType = 0
  Base = -> Fillet003 [Edge6]
  BaseFeature = -> Fillet003
  InvalidShape = false
  NewSolid = false
  Radius = 0.5
  SupportTransform = false
  Suppress = false
  TreeRank = 561
  UseAllEdges = false
  ValidateShape = false
FEATURE [PartDesign::Body] Body003
  AutoGroupSolids = false
  ClaimAllChildren = false
  ExportMode = 0
  Group = -> [Sketch005,Pad002,Sketch006,Import,Import001,Import002,Import003,Import004,Import005,Import006,Import007,Import008,Import009,Import010,Import011,Import012,Import013,Sketch007,Pad003,Pad004,Sketch008,Import014,Import015,Import016,Import017,Pad005,Sketch009,Import018,Sketch010,Import019,Pad006,Pad007,Sketch011,Import020,Pad008,Sketch012,Import021,Pad009,Sketch013,Import022,Pad010,Sketch014,Import023,+20 more]
  InvalidShape = false
  Origin = -> Origin014
  Tip = -> Fillet004
  TreeRank = 490
  ValidateShape = false
  _ExportChildren = -> [Pad002,Import,Import001,Import002,Import003,Import004,Import005,Import006,Import007,Import008,Import009,Import010,Import011,Import012,Import013,Pad003,Pad004,Import014,Import015,Import016,Import017,Pad005,Import018,Import019,Pad006,Pad007,Import020,Pad008,Import021,Pad009,Import022,Pad010,Import023,Pad011,Import024,Pad012,Import025,Pad013,Import026,Import027,Pad014,Pad015,Pocket,Fillet,Fillet001,+3 more]
  _GroupVersion = 1
FEATURE [App::Part] Part010  label="Part"
  ClaimAllChildren = false
  ExportMode = 1
  Group = -> [Body003]
  Origin = -> Origin013
  Placement = pos=(-67,-59.5,0) rot=(0,0,1;0rad)
  TreeRank = 480
  _ExportChildren = -> [Body003]
  _GroupVersion = 1
FEATURE [Mesh::Feature] Mesh001  label="Mesh_Fillets"
  TreeRank = 562
